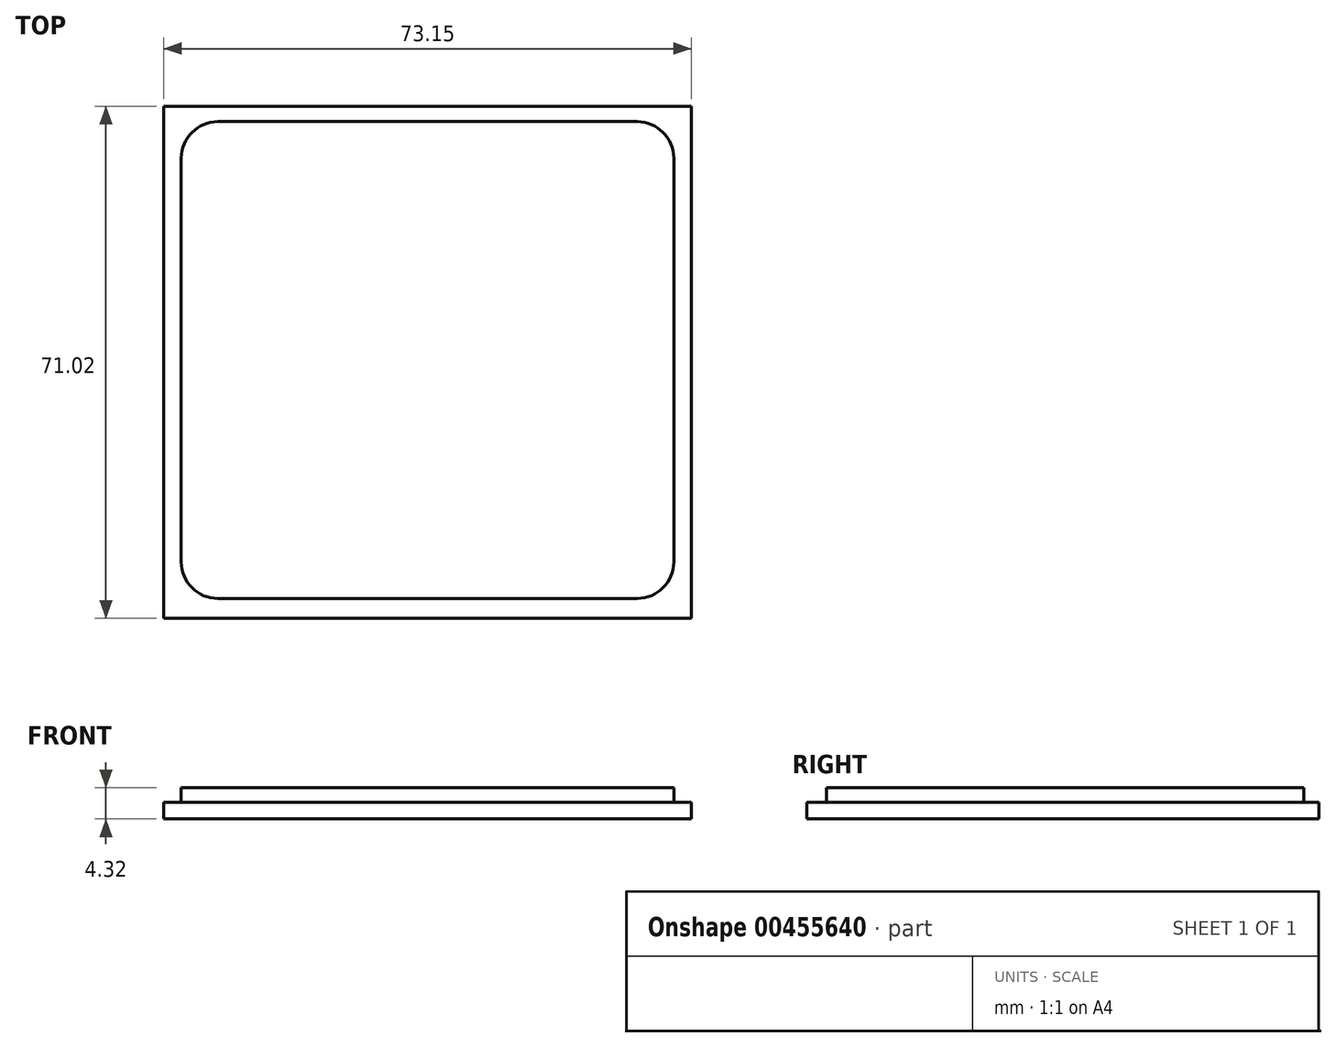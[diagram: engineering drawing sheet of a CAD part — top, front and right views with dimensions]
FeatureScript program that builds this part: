
annotation { "Feature Type Name" : "Feature", "Feature Type Description" : "" }
export const myFeature = defineFeature(function(context is Context, id is Id, definition is map)
    precondition{}
    {
        {
            var Q0;
            Q0=qCreatedBy(makeId("Top.planeOp"),FACE);
            var sketch = newSketch(context, id + "F0", { "sketchPlane" : qUnion([Q0])});
            skLineSegment(sketch, "E0.bottom", {"start": v(-33.83, 37.95) * mm, "end": v(39.32, 37.95) * mm});
            skLineSegment(sketch, "E0.top", {"start": v(-33.83, -33.07) * mm, "end": v(39.32, -33.07) * mm});
            skLineSegment(sketch, "E0.left", {"start": v(-33.83, 37.95) * mm, "end": v(-33.83, -33.07) * mm});
            skLineSegment(sketch, "E0.right", {"start": v(39.32, 37.95) * mm, "end": v(39.32, -33.07) * mm});
            skSolve(sketch);
        }
        {
            var Q0;
            Q0 = qSketchRegion(id + "F0", true);
            extrude(context, id + "F1", {"entities" : qUnion([Q0]), "depth" : 2.3 * mm});
        }
        {
            var Q0;
            Q0=makeQuery(id+"F1.opExtrude","CAP_FACE",FACE,{"disambiguationData":[OSD([sQuery(id+"F0.wireOp",EDGE,"E0.bottom"),sQuery(id+"F0.wireOp",EDGE,"E0.top"),sQuery(id+"F0.wireOp",EDGE,"E0.left"),sQuery(id+"F0.wireOp",EDGE,"E0.right")])],"isStart":false});
            var sketch = newSketch(context, id + "F2", { "sketchPlane" : qUnion([Q0])});
            skSolve(sketch);
        }
        {
            var Q0;
            Q0=makeQuery(id+"F2.imprint","IMPRINT",FACE,{"disambiguationData":[TD([[makeQuery(id+"F2.imprint","IMPRINT",EDGE,{"derivedFrom":makeQuery(id+"F1.opExtrude","CAP_EDGE",EDGE,{"disambiguationData":[OSD([sQuery(id+"F0.wireOp",EDGE,"E0.bottom")])],"isStart":false})}),-1.0]])]});
            var sketch = newSketch(context, id + "F3", { "sketchPlane" : qUnion([Q0])});
            skLineSegment(sketch, "E1.bottom", {"start": v(-31.4, 35.81) * mm, "end": v(36.88, 35.81) * mm});
            skLineSegment(sketch, "E1.top", {"start": v(-31.4, -30.33) * mm, "end": v(36.88, -30.33) * mm});
            skLineSegment(sketch, "E1.left", {"start": v(-31.4, 35.81) * mm, "end": v(-31.4, -30.33) * mm});
            skLineSegment(sketch, "E1.right", {"start": v(36.88, 35.81) * mm, "end": v(36.88, -30.33) * mm});
            skSolve(sketch);
        }
        {
            var Q0;
            Q0=makeQuery(id+"F3.imprint","IMPRINT",FACE,{"disambiguationData":[TD([[makeQuery(id+"F3.imprint","IMPRINT",EDGE,{"derivedFrom":sQuery(id+"F3.wireOp",EDGE,"E1.bottom")}),-1.0]])]});
            extrude(context, id + "F4", {"entities" : qUnion([Q0]), "operationType" : NewBodyOperationType.ADD, "depth" : 2.03 * mm});
        }
        {
            var Q0;
            Q0=makeQuery(id+"F4.opExtrude","SWEPT_EDGE",EDGE,{"disambiguationData":[OSD([sQuery(id+"F3.wireOp",EDGE,"E1.top"),sQuery(id+"F3.wireOp",EDGE,"E1.right")])]});
            fillet(context, id + "F5", {"entities" : qUnion([Q0]), "radius" : 5.08 * mm, "tangentPropagation" : true, "allowEdgeOverflow" : false});
        }
        {
            var Q0;
            Q0=makeQuery(id+"F4.opExtrude","SWEPT_EDGE",EDGE,{"disambiguationData":[OSD([sQuery(id+"F3.wireOp",EDGE,"E1.top"),sQuery(id+"F3.wireOp",EDGE,"E1.left")])]});
            fillet(context, id + "F6", {"entities" : qUnion([Q0]), "radius" : 5.08 * mm, "tangentPropagation" : true, "allowEdgeOverflow" : false});
        }
        {
            var Q0;
            Q0=makeQuery(id+"F4.opExtrude","SWEPT_EDGE",EDGE,{"disambiguationData":[OSD([sQuery(id+"F3.wireOp",EDGE,"E1.bottom"),sQuery(id+"F3.wireOp",EDGE,"E1.left")])]});
            fillet(context, id + "F7", {"entities" : qUnion([Q0]), "radius" : 5.08 * mm, "tangentPropagation" : true, "allowEdgeOverflow" : false});
        }
        {
            var Q0;
            Q0=makeQuery(id+"F4.opExtrude","SWEPT_EDGE",EDGE,{"disambiguationData":[OSD([sQuery(id+"F3.wireOp",EDGE,"E1.bottom"),sQuery(id+"F3.wireOp",EDGE,"E1.right")])]});
            fillet(context, id + "F8", {"entities" : qUnion([Q0]), "radius" : 5.08 * mm, "tangentPropagation" : true, "allowEdgeOverflow" : false});
        }
    });
